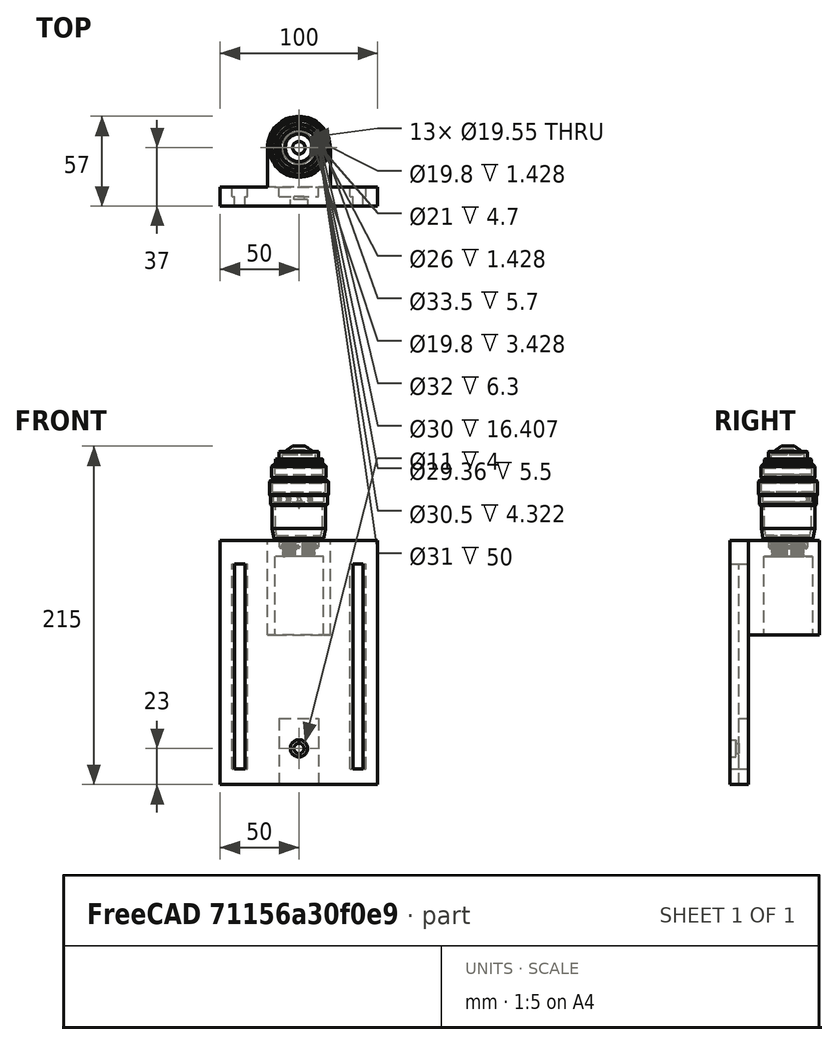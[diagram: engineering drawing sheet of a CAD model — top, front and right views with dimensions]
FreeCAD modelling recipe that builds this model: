
FCSTD DOCUMENT  (FreeCAD 1.0R1.0rc2)
Label: ELP_5_50_CS__Microscope_RMS_Mount
License: All rights reserved
LicenseURL: http://en.wikipedia.org/wiki/All_rights_reserved
objects: Part::Box×7, Part::Cut×6, Part::Cylinder×4, Part::MultiFuse×2, Mesh::Feature×1, Part::Feature×1, Part::FeaturePython×1
note: 21 computed .brp shape members not serialized (recipe doc carries the construction recipe); baked Part::Feature solids carry a one-line shape summary decoded from their .brp

FEATURE [Mesh::Feature] HD_Digital_Cam_ELP_STL_complete  label="HD Digital Cam ELP STL complete"
FEATURE [Part::Feature] Part__Feature  label="Nikon_DIC_N2_Objective"
  Placement = pos=(25,31,215) rot=(1,0,0;-1.5708rad)
  shape: bbox 37.5 x 37.5 x 65.06 mm, 211 faces (baked)
  expr: .Placement.Base.z = 65 + 150
FEATURE [Part::Box] Box  label="Cube"
  AttacherType = Attacher::AttachEngine3D
  Height = 155
  Length = 100
  Placement = pos=(-25,-6,0) rot=(0,0,1;0rad)
  Width = 12
FEATURE [Part::Box] Box001  label="Cube001"
  AttacherType = Attacher::AttachEngine3D
  Height = 60
  Length = 40
  Placement = pos=(5,-4,95) rot=(0,0,1;0rad)
  Width = 35
FEATURE [Part::Cylinder] Cylinder
  Angle = 360
  AttacherType = Attacher::AttachEngine3D
  FirstAngle = 0
  Height = 60
  Placement = pos=(25,31,95) rot=(0,0,1;0rad)
  Radius = 20
  SecondAngle = 0
FEATURE [Part::MultiFuse] Fusion
  Shapes = -> [Cylinder,Box001,Box]
FEATURE [Part::Cylinder] Cylinder001
  Angle = 360
  AttacherType = Attacher::AttachEngine3D
  FirstAngle = 0
  Height = 95
  Placement = pos=(25,31,50) rot=(0,0,1;0rad)
  Radius = 15.5
  SecondAngle = 0
FEATURE [Part::Cut] Cut
  Base = -> Fusion
  Tool = -> Cylinder001
FEATURE [Part::FeaturePython] ScrewTap  label="20.32x20-ScrewTap"  # WARN: FeaturePython — macro-defined, semantics opaque (R4)
  Diameter = 29
  DiameterCustom = 20.32
  Invert = false
  LeftHanded = false
  Length = 20
  MatchOuter = true
  PitchCustom = 0.71
  Placement = pos=(25,31,158) rot=(0,0,1;0rad)
  Thread = true
  Type = 2
FEATURE [Part::Cut] Cut001
  Base = -> Cut
  Tool = -> ScrewTap
FEATURE [Part::Box] Box002  label="Cube002"
  AttacherType = Attacher::AttachEngine3D
  Height = 42
  Length = 25
  Placement = pos=(12.5,0,0) rot=(0,0,1;0rad)
  Width = 6.2
FEATURE [Part::Cut] Cut002
  Base = -> Cut001
  Tool = -> Box002
FEATURE [Part::Cylinder] Cylinder002
  Angle = 360
  AttacherType = Attacher::AttachEngine3D
  FirstAngle = 0
  Height = 100
  Placement = pos=(25,50,23) rot=(1,0,0;1.5708rad)
  Radius = 3.2
  SecondAngle = 0
FEATURE [Part::Cut] Cut003
  Base = -> Cut002
  Tool = -> Cylinder002
FEATURE [Part::Box] Box003  label="Cube003"
  AttacherType = Attacher::AttachEngine3D
  Height = 130
  Length = 6.6
  Placement = pos=(0,-9,10) rot=(0,0,1;0rad)
  Width = 15
FEATURE [Part::Box] Box004  label="Cube004"
  AttacherType = Attacher::AttachEngine3D
  Height = 130
  Length = 6.6
  Placement = pos=(75,-9,10) rot=(0,0,1;0rad)
  Width = 15
FEATURE [Part::Box] Box005  label="Cube005"
  AttacherType = Attacher::AttachEngine3D
  Height = 130
  Length = 10
  Placement = pos=(73.3,0,10) rot=(0,0,1;0rad)
  Width = 6
FEATURE [Part::Box] Box006  label="Cube006"
  AttacherType = Attacher::AttachEngine3D
  Height = 130
  Length = 10
  Placement = pos=(-1.7,0,10) rot=(0,0,1;0rad)
  Width = 6
FEATURE [Part::MultiFuse] Fusion001  label="M6Langloch"
  Placement = pos=(-15.8,0,0) rot=(0,0,1;0rad)
  Shapes = -> [Box004,Box003,Box005,Box006]
FEATURE [Part::Cut] Cut004
  Base = -> Cut003
  Tool = -> Fusion001
FEATURE [Part::Cylinder] Cylinder003
  Angle = 360
  AttacherType = Attacher::AttachEngine3D
  FirstAngle = 0
  Height = 4
  Placement = pos=(25,-2,23) rot=(1,0,0;1.5708rad)
  Radius = 5.5
  SecondAngle = 0
FEATURE [Part::Cut] Cut005
  Base = -> Cut004
  Tool = -> Cylinder003
